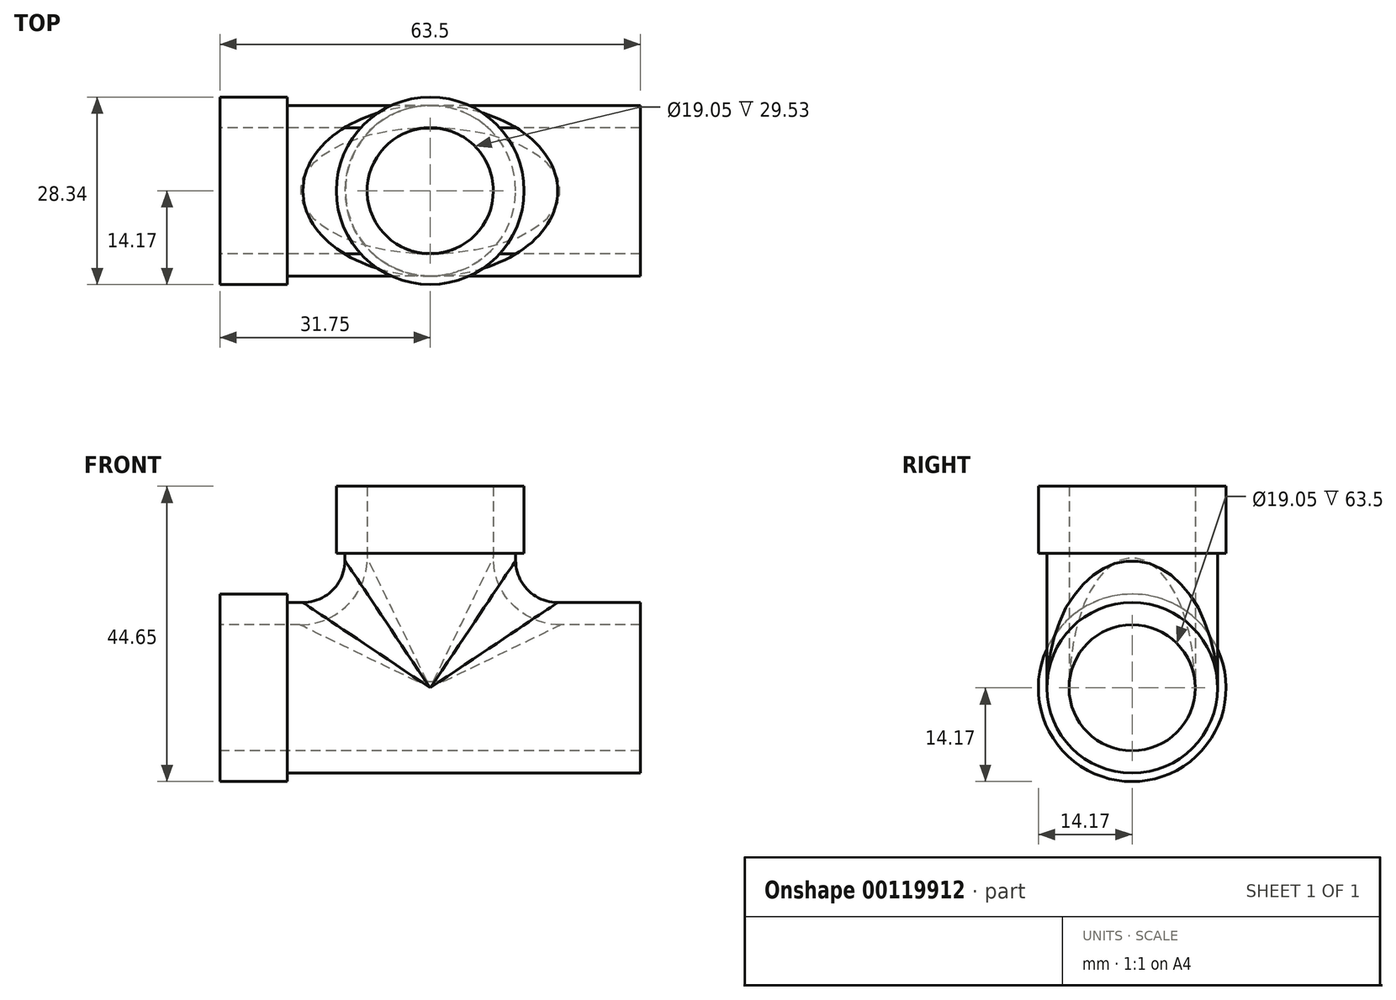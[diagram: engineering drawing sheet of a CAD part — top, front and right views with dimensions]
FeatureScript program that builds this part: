
annotation { "Feature Type Name" : "Feature", "Feature Type Description" : "" }
export const myFeature = defineFeature(function(context is Context, id is Id, definition is map)
    precondition{}
    {
        {
            var Q0;
            Q0=qCreatedBy(makeId("Right.planeOp"),FACE);
            var sketch = newSketch(context, id + "F0", { "sketchPlane" : qUnion([Q0])});
            skCircle(sketch, "E0", {"center": v(0, 0) * mm, "radius": 9.52 * mm});
            skCircle(sketch, "E1", {"center": v(0, 0) * mm, "radius": 12.9 * mm});
            skSolve(sketch);
        }
        {
            var Q0;
            Q0 = qSketchRegion(id + "F0", true);
            extrude(context, id + "F1", {"entities" : qUnion([Q0]), "endBound" : BoundingType.SYMMETRIC, "depth" : 63.5 * mm});
        }
        {
            var Q0;
            Q0=qCreatedBy(makeId("Top.planeOp"),FACE);
            var sketch = newSketch(context, id + "F2", { "sketchPlane" : qUnion([Q0])});
            skCircle(sketch, "E2", {"center": v(0, 0) * mm, "radius": 12.9 * mm});
            skCircle(sketch, "E3", {"center": v(0, 0) * mm, "radius": 9.53 * mm});
            skSolve(sketch);
        }
        {
            var Q0;
            Q0 = qSketchRegion(id + "F2", true);
            extrude(context, id + "F3", {"entities" : qUnion([Q0]), "operationType" : NewBodyOperationType.ADD, "depth" : 30.48 * mm});
        }
        {
            var Q0;
            Q0=makeQuery(id+"F3.boolean.opBoolean","INTERSECT",EDGE,{"disambiguationData":[OD(0.0)],"derivedFrom":[makeQuery(id+"F1.opExtrude","SWEPT_FACE",FACE,{"disambiguationData":[OSD([sQuery(id+"F0.wireOp",EDGE,"E1")])]}),makeQuery(id+"F3.opExtrude","SWEPT_FACE",FACE,{"disambiguationData":[OSD([sQuery(id+"F2.wireOp",EDGE,"E2")])]})]});
            var Q1;
            Q1=makeQuery(id+"F3.boolean.opBoolean","INTERSECT",EDGE,{"disambiguationData":[OD(1.0)],"derivedFrom":[makeQuery(id+"F1.opExtrude","SWEPT_FACE",FACE,{"disambiguationData":[OSD([sQuery(id+"F0.wireOp",EDGE,"E1")])]}),makeQuery(id+"F3.opExtrude","SWEPT_FACE",FACE,{"disambiguationData":[OSD([sQuery(id+"F2.wireOp",EDGE,"E2")])]})]});
            fillet(context, id + "F4", {"entities" : qUnion([Q0, Q1]), "radius" : 6.35 * mm, "tangentPropagation" : true, "allowEdgeOverflow" : false});
        }
        {
            var Q0;
            Q0=makeQuery(id+"F1.opExtrude","CAP_FACE",FACE,{"disambiguationData":[OSD([sQuery(id+"F0.wireOp",EDGE,"E0"),sQuery(id+"F0.wireOp",EDGE,"E1")])],"isStart":true});
            var sketch = newSketch(context, id + "F5", { "sketchPlane" : qUnion([Q0])});
            skCircle(sketch, "E4", {"center": v(0, 0) * mm, "radius": 14.17 * mm});
            skCircle(sketch, "E5.0", {"center": v(0, 0) * mm, "radius": 9.52 * mm});
            skSolve(sketch);
        }
        {
            var Q0;
            Q0 = qSketchRegion(id + "F5", true);
            extrude(context, id + "F6", {"entities" : qUnion([Q0]), "operationType" : NewBodyOperationType.ADD, "oppositeDirection" : true, "depth" : 10.16 * mm});
        }
        {
            var Q0;
            Q0=makeQuery(id+"F6.boolean.opBoolean","MERGE",FACE,{"derivedFrom":[makeQuery(id+"F1.opExtrude","CAP_FACE",FACE,{"disambiguationData":[OSD([sQuery(id+"F0.wireOp",EDGE,"E0"),sQuery(id+"F0.wireOp",EDGE,"E1")])],"isStart":true}),makeQuery(id+"F6.opExtrude","CAP_FACE",FACE,{"disambiguationData":[OSD([sQuery(id+"F5.wireOp",EDGE,"E4"),sQuery(id+"F5.wireOp",EDGE,"E5.0")])],"isStart":true})]});
            var sketch = newSketch(context, id + "F7", { "sketchPlane" : qUnion([Q0])});
            skCircle(sketch, "E6.0", {"center": v(0, 0) * mm, "radius": 9.52 * mm});
            skSolve(sketch);
        }
        {
            var Q0;
            Q0 = qSketchRegion(id + "F7", true);
            extrude(context, id + "F8", {"entities" : qUnion([Q0]), "operationType" : NewBodyOperationType.REMOVE, "endBound" : BoundingType.THROUGH_ALL, "oppositeDirection" : true, "depth" : 25.4 * mm});
        }
        {
            var Q0;
            Q0=makeQuery(id+"F3.opExtrude","CAP_FACE",FACE,{"disambiguationData":[OSD([sQuery(id+"F2.wireOp",EDGE,"E2"),sQuery(id+"F2.wireOp",EDGE,"E3")])],"isStart":false});
            var sketch = newSketch(context, id + "F9", { "sketchPlane" : qUnion([Q0])});
            skCircle(sketch, "E7.0", {"center": v(0, 0) * mm, "radius": 9.53 * mm});
            skSolve(sketch);
        }
        {
            var Q0;
            Q0 = qSketchRegion(id + "F9", true);
            extrude(context, id + "F10", {"entities" : qUnion([Q0]), "operationType" : NewBodyOperationType.REMOVE, "oppositeDirection" : true, "depth" : 29.53 * mm});
        }
        {
            var Q0;
            {var subQ0=sQuery(id+"F0.wireOp",EDGE,"E1");var subQ1=sQuery(id+"F0.wireOp",EDGE,"E0");var subQ2=sQuery(id+"F2.wireOp",EDGE,"E2");var subQ3=makeQuery(id+"F1.opExtrude","SWEPT_FACE",FACE,{"disambiguationData":[OSD([subQ1])]});var subQ4=sQuery(id+"F2.wireOp",EDGE,"E3");var subQ5=makeQuery(id+"F3.opExtrude","CAP_FACE",FACE,{"disambiguationData":[OSD([subQ2,subQ4])],"isStart":true});var subQ6=makeQuery(id+"F3.opExtrude","SWEPT_FACE",FACE,{"disambiguationData":[OSD([subQ4])]});Q0=makeQuery(id+"F10.boolean.opBoolean","INTERSECT",EDGE,{"disambiguationData":[OD(1.0)],"derivedFrom":[makeQuery(id+"F8.boolean.opBoolean","MERGE",FACE,{"derivedFrom":[makeQuery(id+"F3.boolean.opBoolean","SPLIT",FACE,{"disambiguationData":[TD([subQ3,subQ5,subQ6])],"derivedFrom":subQ3}),makeQuery(id+"F3.boolean.opBoolean","SPLIT",FACE,{"disambiguationData":[TD([subQ3,makeQuery(id+"F1.opExtrude","CAP_FACE",FACE,{"disambiguationData":[OSD([subQ1,subQ0])],"isStart":true}),makeQuery(id+"F1.opExtrude","CAP_FACE",FACE,{"disambiguationData":[OSD([subQ1,subQ0])],"isStart":false}),makeQuery(id+"F3.opExtrude","SWEPT_FACE",FACE,{"disambiguationData":[OSD([subQ2])]}),subQ5,subQ6])],"derivedFrom":subQ3}),makeQuery(id+"F8.opExtrude","SWEPT_FACE",FACE,{"disambiguationData":[OSD([sQuery(id+"F7.wireOp",EDGE,"E6.0")])]})]}),makeQuery(id+"F10.opExtrude","SWEPT_FACE",FACE,{"disambiguationData":[OSD([sQuery(id+"F9.wireOp",EDGE,"E7.0")])]})]});}
            var Q1;
            {var subQ0=sQuery(id+"F0.wireOp",EDGE,"E1");var subQ1=sQuery(id+"F0.wireOp",EDGE,"E0");var subQ2=sQuery(id+"F2.wireOp",EDGE,"E2");var subQ3=makeQuery(id+"F1.opExtrude","SWEPT_FACE",FACE,{"disambiguationData":[OSD([subQ1])]});var subQ4=sQuery(id+"F2.wireOp",EDGE,"E3");var subQ5=makeQuery(id+"F3.opExtrude","CAP_FACE",FACE,{"disambiguationData":[OSD([subQ2,subQ4])],"isStart":true});var subQ6=makeQuery(id+"F3.opExtrude","SWEPT_FACE",FACE,{"disambiguationData":[OSD([subQ4])]});Q1=makeQuery(id+"F10.boolean.opBoolean","INTERSECT",EDGE,{"disambiguationData":[OD(0.0)],"derivedFrom":[makeQuery(id+"F8.boolean.opBoolean","MERGE",FACE,{"derivedFrom":[makeQuery(id+"F3.boolean.opBoolean","SPLIT",FACE,{"disambiguationData":[TD([subQ3,subQ5,subQ6])],"derivedFrom":subQ3}),makeQuery(id+"F3.boolean.opBoolean","SPLIT",FACE,{"disambiguationData":[TD([subQ3,makeQuery(id+"F1.opExtrude","CAP_FACE",FACE,{"disambiguationData":[OSD([subQ1,subQ0])],"isStart":true}),makeQuery(id+"F1.opExtrude","CAP_FACE",FACE,{"disambiguationData":[OSD([subQ1,subQ0])],"isStart":false}),makeQuery(id+"F3.opExtrude","SWEPT_FACE",FACE,{"disambiguationData":[OSD([subQ2])]}),subQ5,subQ6])],"derivedFrom":subQ3}),makeQuery(id+"F8.opExtrude","SWEPT_FACE",FACE,{"disambiguationData":[OSD([sQuery(id+"F7.wireOp",EDGE,"E6.0")])]})]}),makeQuery(id+"F10.opExtrude","SWEPT_FACE",FACE,{"disambiguationData":[OSD([sQuery(id+"F9.wireOp",EDGE,"E7.0")])]})]});}
            fillet(context, id + "F11", {"entities" : qUnion([Q0, Q1]), "radius" : 10.16 * mm, "tangentPropagation" : true, "allowEdgeOverflow" : false});
        }
        {
            var Q0;
            Q0=makeQuery(id+"F3.opExtrude","CAP_FACE",FACE,{"disambiguationData":[OSD([sQuery(id+"F2.wireOp",EDGE,"E2"),sQuery(id+"F2.wireOp",EDGE,"E3")])],"isStart":false});
            var sketch = newSketch(context, id + "F12", { "sketchPlane" : qUnion([Q0])});
            skCircle(sketch, "E8.0", {"center": v(0, 0) * mm, "radius": 9.53 * mm});
            skCircle(sketch, "E9", {"center": v(0, 0) * mm, "radius": 14.17 * mm});
            skSolve(sketch);
        }
        {
            var Q0;
            Q0 = qSketchRegion(id + "F12", true);
            extrude(context, id + "F13", {"entities" : qUnion([Q0]), "operationType" : NewBodyOperationType.ADD, "oppositeDirection" : true, "depth" : 10.16 * mm});
        }
    });
